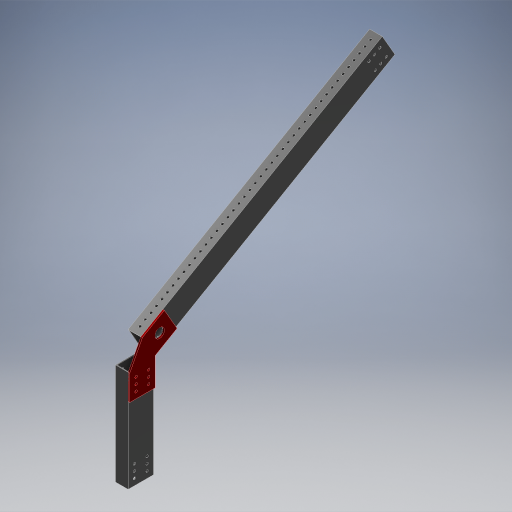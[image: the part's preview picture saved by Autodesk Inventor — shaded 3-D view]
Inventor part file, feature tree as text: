
AUTODESK INVENTOR PART (.ipt)
format: ipt  version: 2024.2 (Build 282272000, 272)  size: 641,024 bytes
history: native  units: in
note: dims shown in document units (in); Inventor stores cm internally (conversion verified against a paired STEP export)
features: extrude x6, sketch x5, projected_geometry x5, other x3
ambient origin geometry x8: Origin, YZ Plane, XZ Plane, XY Plane, X Axis, Y Axis, Z Axis, Center Point
bodies: Body1 (feature_tree), Body2 (feature_tree), Body3 (feature_tree)
feature tree (19):
  other  "2024-210-001-Backright-Support"
  sketch  "Sketch1"  dims[d0=1.0in d1=28.0in]
  extrude  "Extrusion1"  Depth=1.0in
  extrude  "Extrusion2"  Depth=0.196in
  extrude  "Extrusion5"  Depth=0.5in
  extrude  "Extrusion6"  Depth=0.196in
  extrude  "Extrusion7"  Depth=0.125in
  extrude  "Extrusion8"  Depth=0.3937in
  other  "2024-210-002-Angle-Beam"
  sketch  "Sketch3"  dims[d3=26.0in d4=0.196in]
  projected_geometry  "Projected Loop3"
  sketch  "Sketch4"  dims[d5=0.5in d6=0.5in]
  projected_geometry  "Projected Loop4"
  sketch  "Sketch5"  dims[d7=1.1811in d9=0.5in d10=19.2913in d12=0.5in d15=0.196in]
  projected_geometry  "Projected Loop5"
  sketch  "Sketch6"  dims[d16=0.5in d17=0.5in d18=20.8661in d20=0.5in d21=0.3937in d23=1.0in d25=8.0in d26=2.0in d28=2.0in d29=2.0in d31=4.0in d34=0.2in d37=22.0in d38=11.0in d39=0.196in d40=0.5in d41=0.5in d42=0.7874in d44=1.0in d45=1.1811in d47=0.5in d50=0.75in d51=0.196in d52=0.5in d53=0.5in d54=0.7874in d56=1.0in d57=1.1811in d59=0.5in d62=0.196in d63=0.5in d64=0.5in d65=0.7874in d67=1.0in d68=1.1811in d70=0.5in d73=1.0in d74=0.0in d75=1.0in d76=0.0in d79=30.0deg d80=1.0in d81=1.0in d86=0.0625in d87=21.875in d88=0.0in d89=0.0625in d90=0.0in d91=0.0in d92=0.196in d93=0.5in d94=0.5in d95=16.9291in d97=0.5in d98=0.3937in d100=1.0in d102=2.0in d103=0.0in d105=9.0in d106=1.0in d107=-0.1718in d108=2.0in d109=2.0in d110=0.125in d111=0.0in]
  projected_geometry  "Projected Loop6"
  projected_geometry  "Projected Loop7"
  other  "2024-210-003-Dead-Axle-Gusset"
